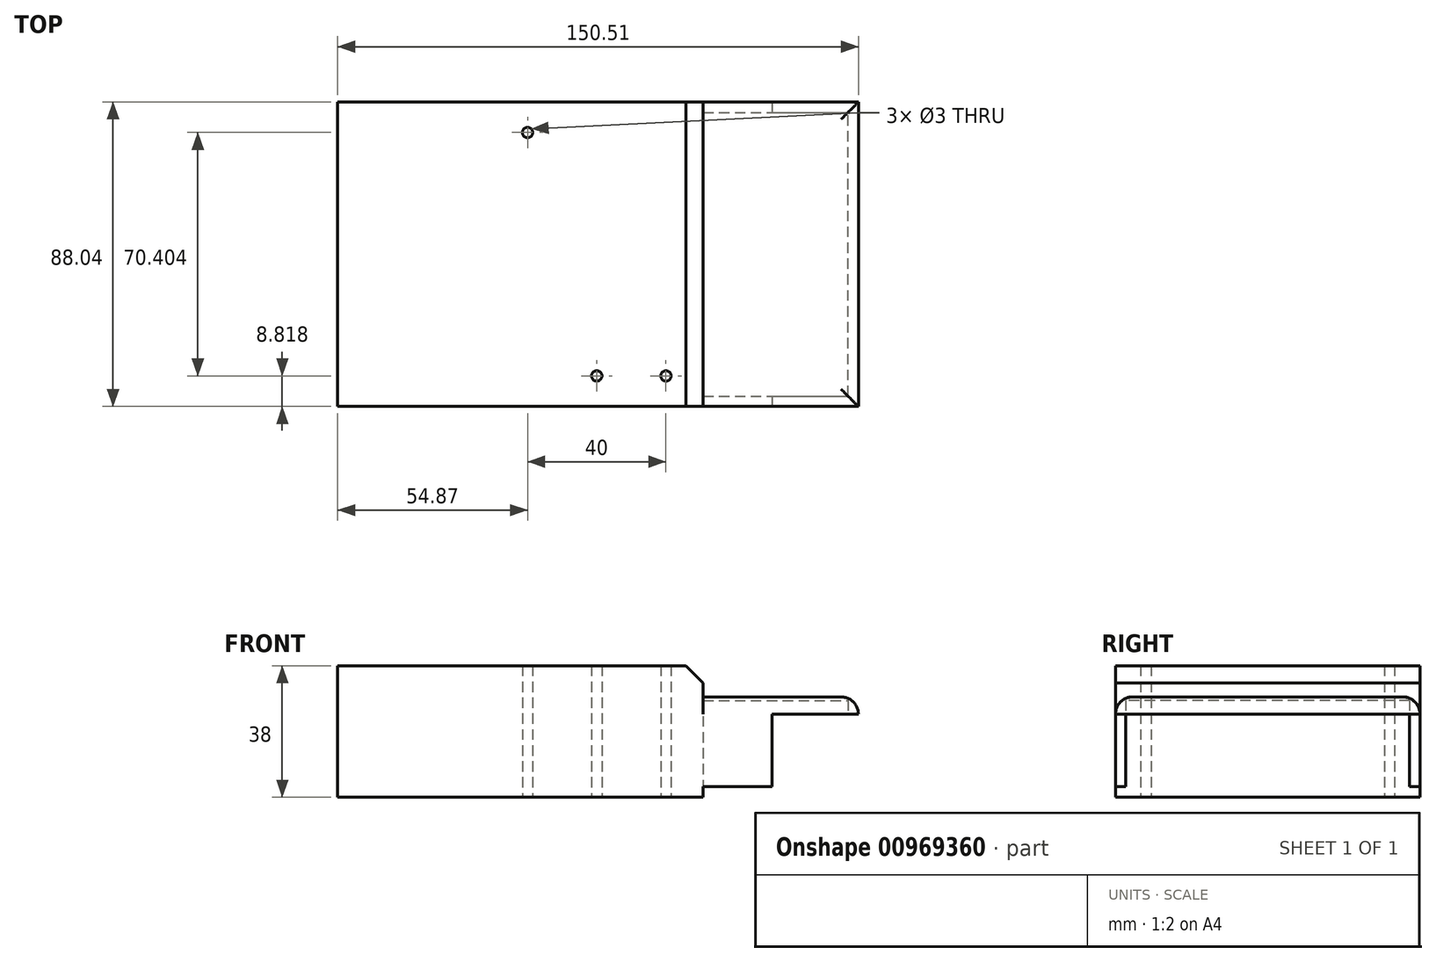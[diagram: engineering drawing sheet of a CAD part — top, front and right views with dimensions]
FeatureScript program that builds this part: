
annotation { "Feature Type Name" : "Feature", "Feature Type Description" : "" }
export const myFeature = defineFeature(function(context is Context, id is Id, definition is map)
    precondition{}
    {
        {
            var Q0;
            Q0=qCreatedBy(makeId("Top.planeOp"),FACE);
            var sketch = newSketch(context, id + "F0", { "sketchPlane" : qUnion([Q0])});
            skLineSegment(sketch, "E0.bottom", {"start": v(-74.87, 44.02) * mm, "end": v(30.76, 44.02) * mm});
            skLineSegment(sketch, "E1.bottom", {"start": v(30.76, 44.02) * mm, "end": v(75.64, 44.02) * mm});
            skLineSegment(sketch, "E2.MirrorCS", {"start": v(-74.87, -44.02) * mm, "end": v(30.76, -44.02) * mm});
            skLineSegment(sketch, "E3.MirrorCS", {"start": v(30.76, -44.02) * mm, "end": v(75.64, -44.02) * mm});
            skLineSegment(sketch, "E4", {"start": v(-74.87, 44.02) * mm, "end": v(-74.87, -44.02) * mm});
            skLineSegment(sketch, "E5", {"start": v(30.76, 44.02) * mm, "end": v(30.76, -44.02) * mm});
            skLineSegment(sketch, "E6", {"start": v(75.64, 44.02) * mm, "end": v(75.64, -44.02) * mm});
            skCircle(sketch, "E7", {"center": v(0, 35.2) * mm, "radius": 1.5 * mm});
            skCircle(sketch, "E8.1.0.0", {"center": v(20, 35.2) * mm, "radius": 1.5 * mm});
            skLineSegment(sketch, "E8.direction1", {"start": v(0, 35.2) * mm, "end": v(20, 35.2) * mm, "construction": true});
            skCircle(sketch, "E9.MirrorC", {"center": v(-20, 35.2) * mm, "radius": 1.5 * mm});
            skCircle(sketch, "E10.MirrorC", {"center": v(-20, -35.2) * mm, "radius": 1.5 * mm});
            skCircle(sketch, "E11.MirrorC", {"center": v(0, -35.2) * mm, "radius": 1.5 * mm});
            skCircle(sketch, "E12.MirrorC", {"center": v(20, -35.2) * mm, "radius": 1.5 * mm});
            skSolve(sketch);
        }
        {
            var Q0;
            Q0=makeQuery(id+"F0.imprint","IMPRINT",FACE,{"disambiguationData":[TD([[makeQuery(id+"F0.imprint","IMPRINT",EDGE,{"derivedFrom":sQuery(id+"F0.wireOp",EDGE,"E0.bottom")}),-1.0]])]});
            var Q1;
            Q1=makeQuery(id+"F0.imprint","IMPRINT",FACE,{"disambiguationData":[TD([[makeQuery(id+"F0.imprint","IMPRINT",EDGE,{"derivedFrom":sQuery(id+"F0.wireOp",EDGE,"E9.MirrorC")}),-1.0]])]});
            var Q2;
            Q2=makeQuery(id+"F0.imprint","IMPRINT",FACE,{"disambiguationData":[TD([[makeQuery(id+"F0.imprint","IMPRINT",EDGE,{"derivedFrom":sQuery(id+"F0.wireOp",EDGE,"E7")}),1.0]])]});
            var Q3;
            Q3=makeQuery(id+"F0.imprint","IMPRINT",FACE,{"disambiguationData":[TD([[makeQuery(id+"F0.imprint","IMPRINT",EDGE,{"derivedFrom":sQuery(id+"F0.wireOp",EDGE,"E8.1.0.0")}),1.0]])]});
            var Q4;
            Q4=makeQuery(id+"F0.imprint","IMPRINT",FACE,{"disambiguationData":[TD([[makeQuery(id+"F0.imprint","IMPRINT",EDGE,{"derivedFrom":sQuery(id+"F0.wireOp",EDGE,"E12.MirrorC")}),-1.0]])]});
            var Q5;
            Q5=makeQuery(id+"F0.imprint","IMPRINT",FACE,{"disambiguationData":[TD([[makeQuery(id+"F0.imprint","IMPRINT",EDGE,{"derivedFrom":sQuery(id+"F0.wireOp",EDGE,"E11.MirrorC")}),-1.0]])]});
            var Q6;
            Q6=makeQuery(id+"F0.imprint","IMPRINT",FACE,{"disambiguationData":[TD([[makeQuery(id+"F0.imprint","IMPRINT",EDGE,{"derivedFrom":sQuery(id+"F0.wireOp",EDGE,"E10.MirrorC")}),1.0]])]});
            extrude(context, id + "F1", {"entities" : qUnion([Q0, Q1, Q2, Q3, Q4, Q5, Q6]), "depth" : 35 * mm, "offsetDistance" : 25 * mm});
        }
        {
            var Q0;
            Q0=makeQuery(id+"F0.imprint","IMPRINT",FACE,{"disambiguationData":[TD([[makeQuery(id+"F0.imprint","IMPRINT",EDGE,{"derivedFrom":sQuery(id+"F0.wireOp",EDGE,"E1.bottom")}),-1.0]])]});
            extrude(context, id + "F2", {"entities" : qUnion([Q0]), "operationType" : NewBodyOperationType.ADD, "depth" : 26 * mm, "offsetDistance" : 25 * mm});
        }
        {
            var Q0;
            Q0=makeQuery(id+"F1.opExtrude","CAP_EDGE",EDGE,{"disambiguationData":[OSD([sQuery(id+"F0.wireOp",EDGE,"E5")])],"isStart":false});
            chamfer(context, id + "F3", {"entities" : qUnion([Q0]), "width" : 5 * mm, "tangentPropagation" : true});
        }
        {
            var Q0;
            Q0=qCreatedBy(makeId("Top.planeOp"),FACE);
            var sketch = newSketch(context, id + "F4", { "sketchPlane" : qUnion([Q0])});
            skLineSegment(sketch, "E13.bottom", {"start": v(-71.87, -41.02) * mm, "end": v(72.64, -41.02) * mm});
            skLineSegment(sketch, "E13.top", {"start": v(-71.87, 41.02) * mm, "end": v(72.64, 41.02) * mm});
            skLineSegment(sketch, "E13.left", {"start": v(-71.87, -41.02) * mm, "end": v(-71.87, 41.02) * mm});
            skLineSegment(sketch, "E13.right", {"start": v(72.64, -41.02) * mm, "end": v(72.64, 41.02) * mm});
            skLineSegment(sketch, "E14", {"start": v(30.71, -41.02) * mm, "end": v(30.71, 41.02) * mm});
            skSolve(sketch);
        }
        {
            var Q0;
            Q0 = qSketchRegion(id + "F4", true);
            extrude(context, id + "F5", {"entities" : qUnion([Q0]), "operationType" : NewBodyOperationType.REMOVE, "depth" : 25 * mm, "offsetDistance" : 25 * mm});
        }
        {
            var Q0;
            Q0=makeQuery(id+"F2.opExtrude","CAP_EDGE",EDGE,{"disambiguationData":[OSD([sQuery(id+"F0.wireOp",EDGE,"E3.MirrorCS")])],"isStart":false});
            var Q1;
            Q1=makeQuery(id+"F2.opExtrude","CAP_EDGE",EDGE,{"disambiguationData":[OSD([sQuery(id+"F0.wireOp",EDGE,"E6")])],"isStart":false});
            var Q2;
            Q2=makeQuery(id+"F2.opExtrude","CAP_EDGE",EDGE,{"disambiguationData":[OSD([sQuery(id+"F0.wireOp",EDGE,"E1.bottom")])],"isStart":false});
            fillet(context, id + "F6", {"entities" : qUnion([Q0, Q1, Q2]), "radius" : 5 * mm, "tangentPropagation" : true, "allowEdgeOverflow" : false});
        }
        {
            var Q0;
            Q0=makeQuery(id+"F1.opExtrude","SWEPT_FACE",FACE,{"disambiguationData":[OSD([sQuery(id+"F0.wireOp",EDGE,"E4")])]});
            var sketch = newSketch(context, id + "F7", { "sketchPlane" : qUnion([Q0])});
            skLineSegment(sketch, "E15.bottom", {"start": v(-30.5, 0) * mm, "end": v(9.05, 0) * mm});
            skLineSegment(sketch, "E16.bottom", {"start": v(-30.43, 3) * mm, "end": v(19.57, 3) * mm});
            skLineSegment(sketch, "E16.top", {"start": v(-30.43, 17) * mm, "end": v(19.57, 17) * mm});
            skLineSegment(sketch, "E16.left", {"start": v(-30.43, 3) * mm, "end": v(-30.43, 17) * mm});
            skLineSegment(sketch, "E16.right", {"start": v(19.57, 3) * mm, "end": v(19.57, 17) * mm});
            skSolve(sketch);
        }
        {
            var Q0;
            Q0=makeQuery(id+"F7.imprint","IMPRINT",FACE,{"disambiguationData":[TD([[makeQuery(id+"F7.imprint","IMPRINT",EDGE,{"derivedFrom":sQuery(id+"F7.wireOp",EDGE,"E16.bottom")}),1.0]])]});
            extrude(context, id + "F8", {"entities" : qUnion([Q0]), "operationType" : NewBodyOperationType.REMOVE, "oppositeDirection" : true, "depth" : 3 * mm, "offsetDistance" : 25 * mm});
        }
        {
            var Q0;
            Q0=makeQuery(id+"F0.imprint","IMPRINT",FACE,{"disambiguationData":[TD([[makeQuery(id+"F0.imprint","IMPRINT",EDGE,{"derivedFrom":sQuery(id+"F0.wireOp",EDGE,"E10.MirrorC")}),1.0]])]});
            var Q1;
            Q1=makeQuery(id+"F0.imprint","IMPRINT",FACE,{"disambiguationData":[TD([[makeQuery(id+"F0.imprint","IMPRINT",EDGE,{"derivedFrom":sQuery(id+"F0.wireOp",EDGE,"E11.MirrorC")}),-1.0]])]});
            var Q2;
            Q2=makeQuery(id+"F0.imprint","IMPRINT",FACE,{"disambiguationData":[TD([[makeQuery(id+"F0.imprint","IMPRINT",EDGE,{"derivedFrom":sQuery(id+"F0.wireOp",EDGE,"E12.MirrorC")}),-1.0]])]});
            var Q3;
            Q3=makeQuery(id+"F0.imprint","IMPRINT",FACE,{"disambiguationData":[TD([[makeQuery(id+"F0.imprint","IMPRINT",EDGE,{"derivedFrom":sQuery(id+"F0.wireOp",EDGE,"E9.MirrorC")}),-1.0]])]});
            var Q4;
            Q4=makeQuery(id+"F0.imprint","IMPRINT",FACE,{"disambiguationData":[TD([[makeQuery(id+"F0.imprint","IMPRINT",EDGE,{"derivedFrom":sQuery(id+"F0.wireOp",EDGE,"E8.1.0.0")}),1.0]])]});
            var Q5;
            Q5=makeQuery(id+"F0.imprint","IMPRINT",FACE,{"disambiguationData":[TD([[makeQuery(id+"F0.imprint","IMPRINT",EDGE,{"derivedFrom":sQuery(id+"F0.wireOp",EDGE,"E7")}),1.0]])]});
            extrude(context, id + "F9", {"entities" : qUnion([Q0, Q1, Q2, Q3, Q4, Q5]), "operationType" : NewBodyOperationType.ADD, "depth" : 25 * mm, "offsetDistance" : 25 * mm, "hasSecondDirection" : true, "secondDirectionOppositeDirection" : true, "secondDirectionDepth" : 3 * mm});
        }
        {
            var Q0;
            Q0=makeQuery(id+"F2.opExtrude","SWEPT_FACE",FACE,{"disambiguationData":[OSD([sQuery(id+"F0.wireOp",EDGE,"E6")])]});
            var sketch = newSketch(context, id + "F10", { "sketchPlane" : qUnion([Q0])});
            skLineSegment(sketch, "E17.bottom", {"start": v(-44.02, 0) * mm, "end": v(44.02, 0) * mm});
            skLineSegment(sketch, "E17.top", {"start": v(-44.02, 21) * mm, "end": v(44.02, 21) * mm});
            skLineSegment(sketch, "E17.left", {"start": v(-44.02, 0) * mm, "end": v(-44.02, 21) * mm});
            skLineSegment(sketch, "E17.right", {"start": v(44.02, 0) * mm, "end": v(44.02, 21) * mm});
            skSolve(sketch);
        }
        {
            var Q0;
            Q0=makeQuery(id+"F10.imprint","IMPRINT",FACE,{"disambiguationData":[TD([[makeQuery(id+"F10.imprint","IMPRINT",EDGE,{"derivedFrom":sQuery(id+"F10.wireOp",EDGE,"E17.bottom")}),-1.0]])]});
            extrude(context, id + "F11", {"entities" : qUnion([Q0]), "operationType" : NewBodyOperationType.REMOVE, "oppositeDirection" : true, "depth" : 25 * mm, "offsetDistance" : 25 * mm});
        }
    });
